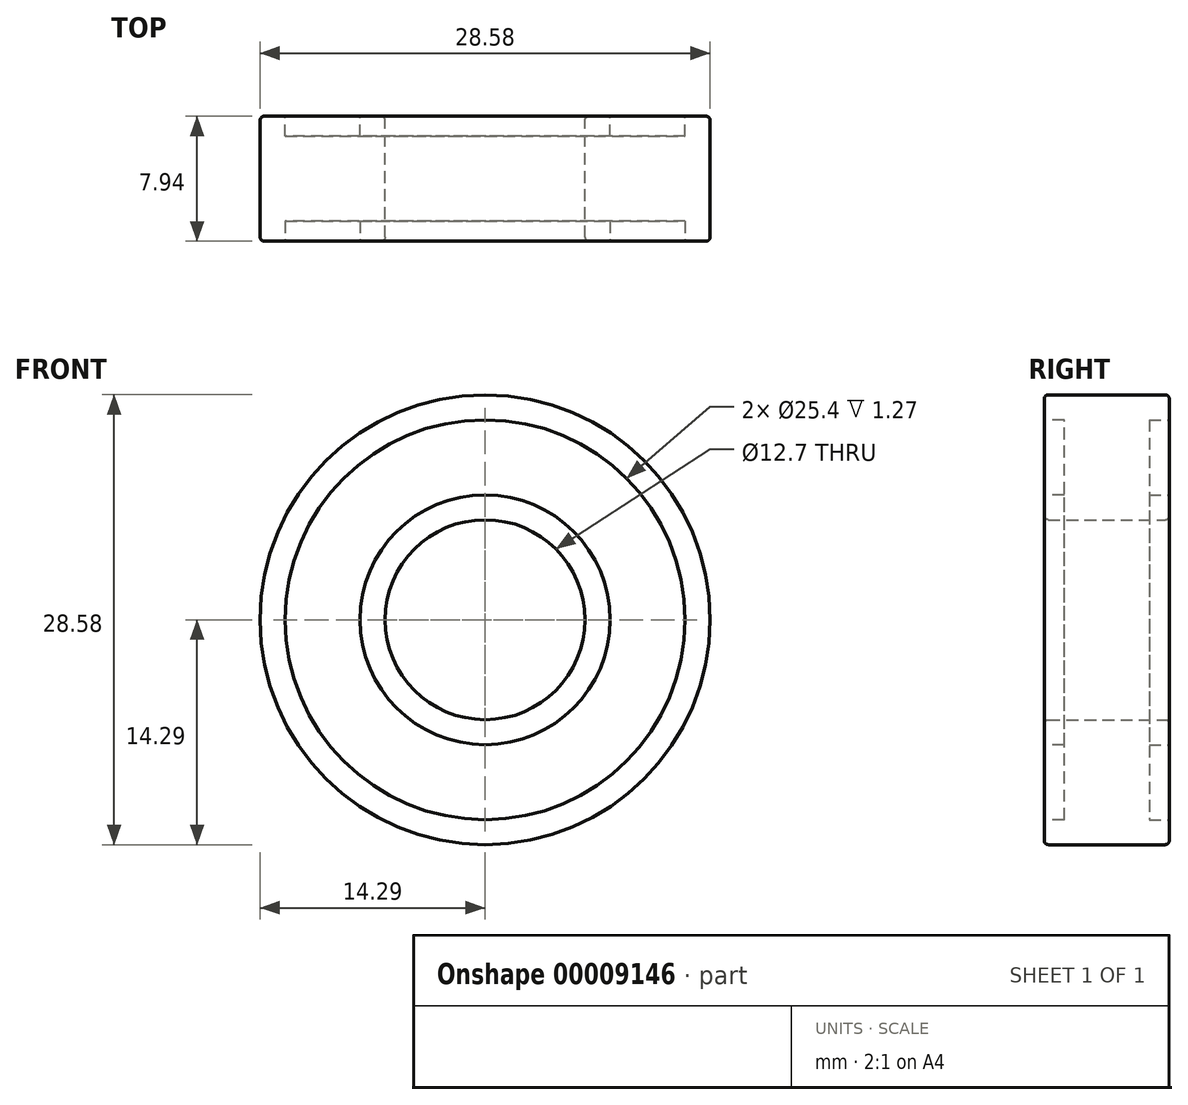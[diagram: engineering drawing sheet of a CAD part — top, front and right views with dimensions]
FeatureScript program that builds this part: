
annotation { "Feature Type Name" : "Feature", "Feature Type Description" : "" }
export const myFeature = defineFeature(function(context is Context, id is Id, definition is map)
    precondition{}
    {
        {
            var Q0;
            Q0=qCreatedBy(makeId("Front.planeOp"),FACE);
            var sketch = newSketch(context, id + "F0", { "sketchPlane" : qUnion([Q0])});
            skCircle(sketch, "E0", {"center": v(0, 0) * mm, "radius": 14.29 * mm});
            skCircle(sketch, "E1", {"center": v(0, 0) * mm, "radius": 6.35 * mm});
            skCircle(sketch, "E2", {"center": v(0, 0) * mm, "radius": 7.94 * mm});
            skCircle(sketch, "E3", {"center": v(0, 0) * mm, "radius": 12.7 * mm});
            skSolve(sketch);
        }
        {
            var Q0;
            Q0=makeQuery(id+"F0.imprint","IMPRINT",FACE,{"disambiguationData":[TD([[makeQuery(id+"F0.imprint","IMPRINT",EDGE,{"derivedFrom":sQuery(id+"F0.wireOp",EDGE,"E0")}),1.0]])]});
            var Q1;
            Q1=makeQuery(id+"F0.imprint","IMPRINT",FACE,{"disambiguationData":[TD([[makeQuery(id+"F0.imprint","IMPRINT",EDGE,{"derivedFrom":sQuery(id+"F0.wireOp",EDGE,"E2")}),-1.0]])]});
            var Q2;
            Q2=makeQuery(id+"F0.imprint","IMPRINT",FACE,{"disambiguationData":[TD([[makeQuery(id+"F0.imprint","IMPRINT",EDGE,{"derivedFrom":sQuery(id+"F0.wireOp",EDGE,"E1")}),-1.0]])]});
            extrude(context, id + "F1", {"entities" : qUnion([Q0, Q1, Q2]), "depth" : 7.94 * mm});
        }
        {
            var Q0;
            Q0=makeQuery(id+"F1.opExtrude","CAP_FACE",FACE,{"disambiguationData":[OSD([sQuery(id+"F0.wireOp",EDGE,"E0"),sQuery(id+"F0.wireOp",EDGE,"E1")])],"isStart":false});
            var sketch = newSketch(context, id + "F2", { "sketchPlane" : qUnion([Q0])});
            skCircle(sketch, "E4", {"center": v(0, 0) * mm, "radius": 7.94 * mm});
            skCircle(sketch, "E5", {"center": v(0, 0) * mm, "radius": 12.7 * mm});
            skSolve(sketch);
        }
        {
            var Q0;
            Q0=makeQuery(id+"F2.imprint","IMPRINT",FACE,{"disambiguationData":[TD([[makeQuery(id+"F2.imprint","IMPRINT",EDGE,{"derivedFrom":sQuery(id+"F2.wireOp",EDGE,"E4")}),-1.0]])]});
            extrude(context, id + "F3", {"entities" : qUnion([Q0]), "operationType" : NewBodyOperationType.REMOVE, "oppositeDirection" : true, "depth" : 1.27 * mm});
        }
        {
            var Q0;
            Q0=makeQuery(id+"F1.opExtrude","CAP_EDGE",EDGE,{"disambiguationData":[OSD([sQuery(id+"F0.wireOp",EDGE,"E0")])],"isStart":false});
            var Q1;
            Q1=makeQuery(id+"F1.opExtrude","CAP_EDGE",EDGE,{"disambiguationData":[OSD([sQuery(id+"F0.wireOp",EDGE,"E1")])],"isStart":false});
            fillet(context, id + "F4", {"entities" : qUnion([Q0, Q1]), "radius" : 0.25 * mm, "tangentPropagation" : true, "allowEdgeOverflow" : false});
        }
        {
            var Q0;
            Q0=makeQuery(id+"F1.opExtrude","CAP_FACE",FACE,{"disambiguationData":[OSD([sQuery(id+"F0.wireOp",EDGE,"E0"),sQuery(id+"F0.wireOp",EDGE,"E1")])],"isStart":true});
            var sketch = newSketch(context, id + "F5", { "sketchPlane" : qUnion([Q0])});
            skCircle(sketch, "E6", {"center": v(0, 0) * mm, "radius": 7.94 * mm});
            skCircle(sketch, "E7", {"center": v(0, 0) * mm, "radius": 12.7 * mm});
            skSolve(sketch);
        }
        {
            var Q0;
            Q0=makeQuery(id+"F5.imprint","IMPRINT",FACE,{"disambiguationData":[TD([[makeQuery(id+"F5.imprint","IMPRINT",EDGE,{"derivedFrom":sQuery(id+"F5.wireOp",EDGE,"E6")}),-1.0]])]});
            extrude(context, id + "F6", {"entities" : qUnion([Q0]), "operationType" : NewBodyOperationType.REMOVE, "oppositeDirection" : true, "depth" : 1.27 * mm});
        }
        {
            var Q0;
            Q0=makeQuery(id+"F1.opExtrude","CAP_EDGE",EDGE,{"disambiguationData":[OSD([sQuery(id+"F0.wireOp",EDGE,"E0")])],"isStart":true});
            var Q1;
            Q1=makeQuery(id+"F1.opExtrude","CAP_EDGE",EDGE,{"disambiguationData":[OSD([sQuery(id+"F0.wireOp",EDGE,"E1")])],"isStart":true});
            fillet(context, id + "F7", {"entities" : qUnion([Q0, Q1]), "radius" : 0.25 * mm, "tangentPropagation" : true, "allowEdgeOverflow" : false});
        }
    });
